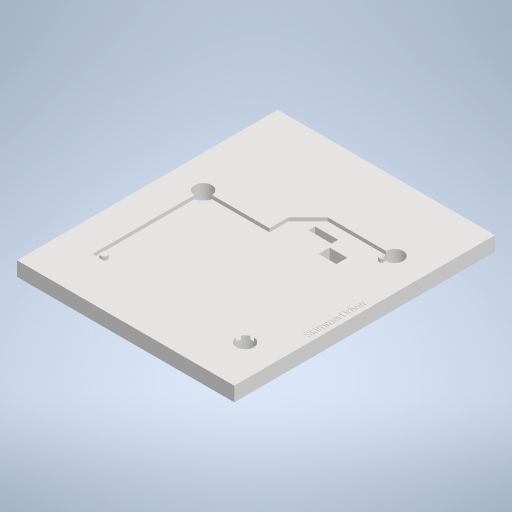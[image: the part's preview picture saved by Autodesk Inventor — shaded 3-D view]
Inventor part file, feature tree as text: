
AUTODESK INVENTOR PART (.ipt)
format: ipt  version: 2023.2 (Build 272271000, 271)  size: 565,760 bytes
history: native  units: in
note: dims shown in document units (in); Inventor stores cm internally (conversion verified against a paired STEP export)
features: reference x6, sketch x4, other x4, extrude x3, emboss x1
ambient origin geometry x8: Origin, YZ Plane, XZ Plane, XY Plane, X Axis, Y Axis, Z Axis, Center Point
bodies: Solid1 (feature_tree)
feature tree (18):
  extrude  "Extrusion1"  Depth=3.937in
  extrude  "Extrusion2"  Depth=0.0039in
  extrude  "Extrusion3"  Depth=0.0039in
  emboss  "Emboss1"
  sketch  "Sketch1"  dims[d0=4.7244in d1=3.937in]
  sketch  "Sketch2"  dims[d2=0.1969in d3=0.0in d4=0.0039in]
  reference  "Reference1"
  sketch  "Sketch3"  dims[d5=0.0039in d6=0.0039in]
  reference  "Reference2"
  reference  "Reference3"
  reference  "Reference4"
  reference  "Reference5"
  reference  "Reference6"
  sketch  "Sketch4"  dims[d7=0.0039in d8=0.063in d9=0.0in d10=0.315in d11=0.0591in d12=0.0591in d13=0.0591in d14=0.0591in d15=0.0591in d16=0.0591in d17=0.0591in d18=0.0591in d19=0.0in d20=0.0in d21=0.0079in d22=0.0in]
  other  "<userpath>\Dropbox\elec\Mechanical\SkimmerSwabbie\_Tooling_PCBPaste.iam"
  other  "_Tooling_PCBPaste.iam"
  other  "skimmer_swabbie_v1:1"
  other  "skimmer_swabbie_v1_BOARD:1"
